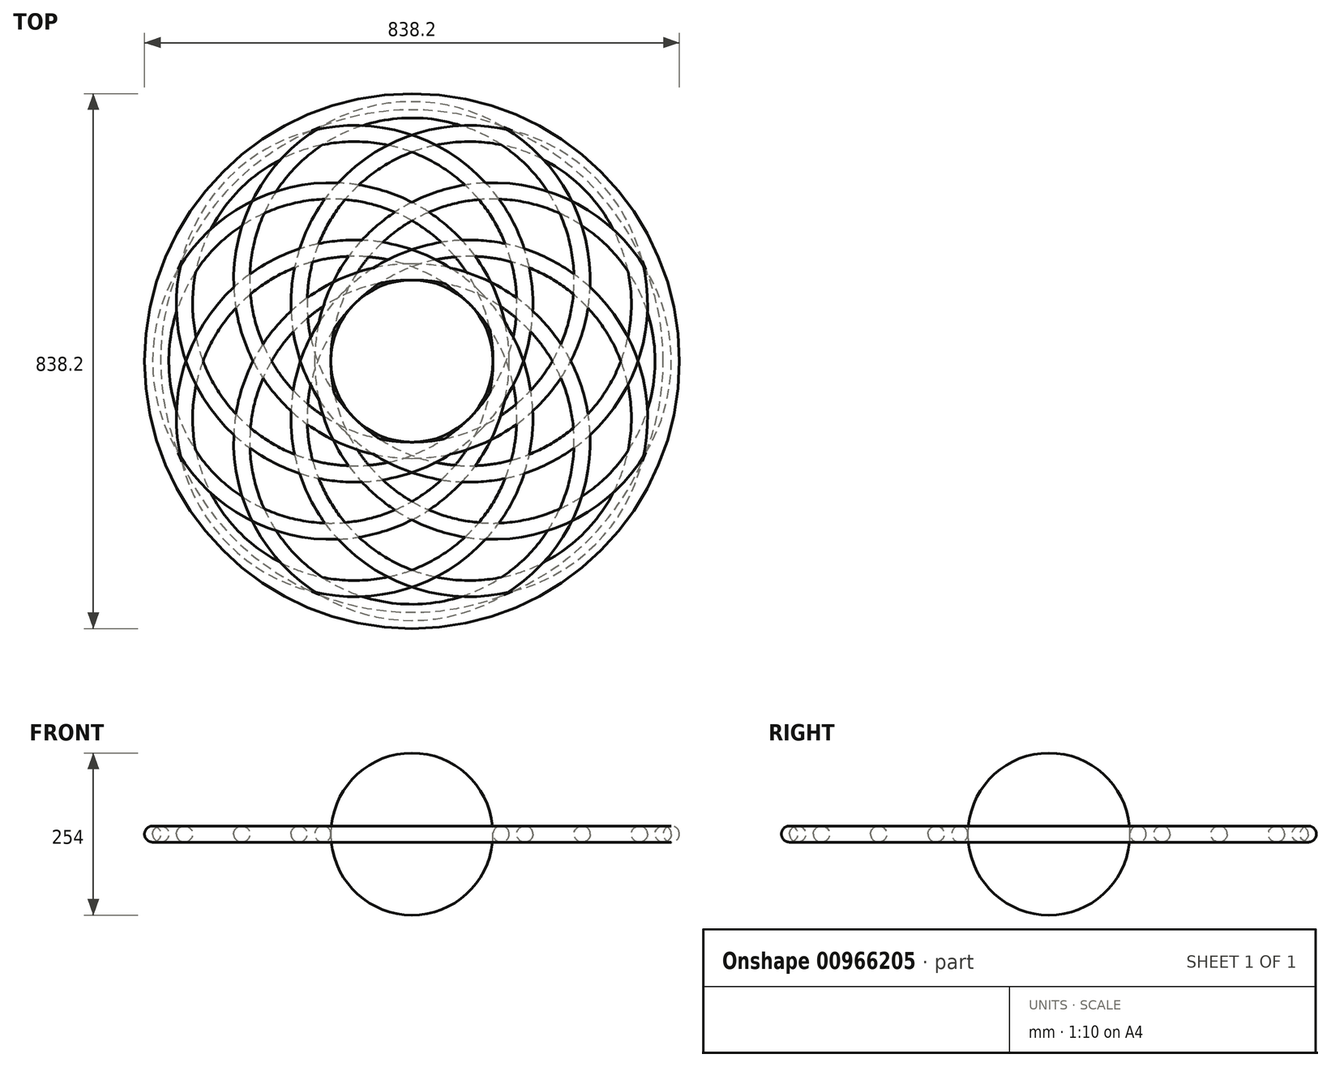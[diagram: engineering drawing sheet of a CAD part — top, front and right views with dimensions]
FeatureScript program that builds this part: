
annotation { "Feature Type Name" : "Feature", "Feature Type Description" : "" }
export const myFeature = defineFeature(function(context is Context, id is Id, definition is map)
    precondition{}
    {
        {
            var Q0;
            Q0=qCreatedBy(makeId("Top.planeOp"),FACE);
            var sketch = newSketch(context, id + "F0", { "sketchPlane" : qUnion([Q0])});
            skArc(sketch, "E0", {"start": v(0, -127) * mm, "mid": v(127, 0) * mm, "end": v(0, 127) * mm});
            skLineSegment(sketch, "E1", {"start": v(0, 127) * mm, "end": v(0, -127) * mm});
            skSolve(sketch);
        }
        {
            var Q0;
            Q0=qSketchRegion(id+"F0",true);
            var Q1;
            Q1=sQuery(id+"F0.wireOp",EDGE,"E1");
            revolve(context, id + "F1", {"surfaceOperationType" : NewSurfaceOperationType.NEW, "entities" : qUnion([Q0]), "axis" : qUnion([Q1]), "revolveType" : RevolveType.FULL});
        }
        {
            var Q0;
            Q0=qCreatedBy(makeId("Top.planeOp"),FACE);
            var sketch = newSketch(context, id + "F2", { "sketchPlane" : qUnion([Q0])});
            skCircle(sketch, "E2", {"center": v(-127, 0) * mm, "radius": 254 * mm});
            skArc(sketch, "E3.0", {"start": v(0, -127) * mm, "mid": v(127, 0) * mm, "end": v(0, 127) * mm});
            skCircle(sketch, "E4.0", {"center": v(-127, 0) * mm, "radius": 266.7 * mm});
            skSolve(sketch);
        }
        {
            var Q0;
            Q0=qCreatedBy(makeId("Top.planeOp"),FACE);
            var sketch = newSketch(context, id + "F3", { "sketchPlane" : qUnion([Q0])});
            skCircle(sketch, "E5.0", {"center": v(-127, 0) * mm, "radius": 266.7 * mm});
            skSolve(sketch);
        }
        {
            var Q0;
            Q0=qCreatedBy(makeId("Front.planeOp"),FACE);
            var sketch = newSketch(context, id + "F4", { "sketchPlane" : qUnion([Q0])});
            skCircle(sketch, "E6", {"center": v(139.7, 0) * mm, "radius": 12.7 * mm});
            skLineSegment(sketch, "E7.0", {"start": v(-393.7, 0) * mm, "end": v(139.7, 0) * mm});
            skLineSegment(sketch, "E8.0", {"start": v(-381, 0) * mm, "end": v(127, 0) * mm});
            skSolve(sketch);
        }
        {
            var Q0;
            Q0=makeQuery(id+"F4.imprint","IMPRINT",FACE,{"disambiguationData":[TD([[makeQuery(id+"F4.imprint","IMPRINT",EDGE,{"derivedFrom":sQuery(id+"F4.wireOp",EDGE,"E6")}),1.0]])]});
            var Q1;
            Q1=sQuery(id+"F3.wireOp",EDGE,"E5.0");
            sweep(context, id + "F5", {"profiles" : qUnion([Q0]), "path" : qUnion([Q1])});
        }
        {
            var Q0;
            Q0=qCreatedBy(makeId("Right.planeOp"),FACE);
            var sketch = newSketch(context, id + "F6", { "sketchPlane" : qUnion([Q0])});
            skLineSegment(sketch, "E9", {"start": v(0, -32) * mm, "end": v(0, 125.32) * mm});
            skSolve(sketch);
        }
        {
            var Q0;
            Q0=makeQuery(id+"F5.opSweep","SWEPT_BODY",BODY,{"disambiguationData":[OSD([sQuery(id+"F3.wireOp",EDGE,"E5.0"),sQuery(id+"F4.wireOp",EDGE,"E6")])]});
            var Q1;
            Q1=sQuery(id+"F6.wireOp",EDGE,"E9");
            circularPattern(context, id + "F7", {"entities" : qUnion([Q0]), "axis" : qUnion([Q1]), "angle" : 360 * degree, "instanceCount" : 8, "equalSpace" : true});
        }
        {
            var Q0;
            Q0=qCreatedBy(makeId("Top.planeOp"),FACE);
            var sketch = newSketch(context, id + "F8", { "sketchPlane" : qUnion([Q0])});
            skCircle(sketch, "E10", {"center": v(0, -127) * mm, "radius": 254 * mm});
            skCircle(sketch, "E11", {"center": v(89.8, 89.8) * mm, "radius": 279.4 * mm});
            skCircle(sketch, "E12", {"center": v(89.8, 89.8) * mm, "radius": 254 * mm});
            skCircle(sketch, "E13", {"center": v(0, -127) * mm, "radius": 279.4 * mm});
            skCircle(sketch, "E14", {"center": v(-89.8, 89.8) * mm, "radius": 279.4 * mm});
            skCircle(sketch, "E15", {"center": v(-89.8, 89.8) * mm, "radius": 254 * mm});
            skSolve(sketch);
        }
        {
            var Q0;
            Q0=qCreatedBy(makeId("Top.planeOp"),FACE);
            var sketch = newSketch(context, id + "F9", { "sketchPlane" : qUnion([Q0])});
            skArc(sketch, "E16.0", {"start": v(0, -127) * mm, "mid": v(127, 0) * mm, "end": v(0, 127) * mm});
            skCircle(sketch, "E17.0", {"center": v(0, -127) * mm, "radius": 254 * mm});
            skCircle(sketch, "E18.0", {"center": v(0, -127) * mm, "radius": 279.4 * mm});
            skCircle(sketch, "E19.0", {"center": v(89.8, 89.8) * mm, "radius": 279.4 * mm});
            skCircle(sketch, "E20.0", {"center": v(-89.8, 89.8) * mm, "radius": 279.4 * mm});
            skCircle(sketch, "E21", {"center": v(0, 0) * mm, "radius": 406.4 * mm});
            skSolve(sketch);
        }
        {
            var Q0;
            Q0=qCreatedBy(makeId("Front.planeOp"),FACE);
            var sketch = newSketch(context, id + "F10", { "sketchPlane" : qUnion([Q0])});
            skLineSegment(sketch, "E22.0", {"start": v(-406.4, 0) * mm, "end": v(406.4, 0) * mm});
            skCircle(sketch, "E23", {"center": v(406.4, 0) * mm, "radius": 12.7 * mm});
            skSolve(sketch);
        }
        {
            var Q0;
            Q0=makeQuery(id+"F10.imprint","IMPRINT",FACE,{"disambiguationData":[TD([[makeQuery(id+"F10.imprint","IMPRINT",EDGE,{"derivedFrom":sQuery(id+"F10.wireOp",EDGE,"E23")}),1.0]])]});
            var Q1;
            Q1=sQuery(id+"F9.wireOp",EDGE,"E21");
            sweep(context, id + "F11", {"profiles" : qUnion([Q0]), "path" : qUnion([Q1])});
        }
    });
